# Revit family: 1STERN_FAUCET_TOUCHLESS_APOLLO_MEDICAL_F
name_source: partatom
category: Generic Models
revit_build: Autodesk Revit 2017 (Build: 20160225_1515(x64)
units: mm (PartAtom-declared; Revit-internal decimal feet)

## family parameters
Can host rebar = No
Cut with Voids When Loaded = No
Host = Face
Part Type = Normal
Room Calculation Point = Yes
Round Connector Dimension = Use Diameter
Shared = No

## types (2) — shared parameters
AVAILABLE FINISHES = Brushed Nickel - Matt Black - Satin Gold - PVD Antique Bronze - PVD rose Gold - PVD Copper - AISI316 Material
BADGE = https://bim.archiproducts.com
DEPTH = 255 mm  [stored 0.836614 ft]
Default Elevation = 1219 mm
Description = Apollo Medical F - Touch-free wall-mounted electronic faucet.‎ For hot and cold water, includes a mixer for temperature adjustment.‎ Gooseneck spout.‎ Powered by an internal 9V battery.‎ Includes a low battery indicator.‎ Adjustable settings by remote control: security time, delay in, delay out, on-off and reset to factory settings.‎
FINISHING MATERIAL = Chrome - Stern
HEIGHT = 260 mm  [stored 0.853018 ft]
INSTALLATION = Exposed wall mounted
MATERIAL DESCRIPTION = Finish: Chrome
Manufacturer = Stern Engineering
OPERATING PRESSURE = 0.5 - 5.0 BAR (7- 72.5  PSI). For water pressure greater than 5.0 bar use a pressure reducing valve.
OPTIONS = Remote control (code 07100005)
PRODUCT SHEET = https://www.archiproducts.com
SECURITY TIME = 90 seconds. Adjustableby remote control.
TECHNICAL SHEET = http://www.sternfaucets.com
URL = http://www.sternfaucets.com
VOLTAGE = 9 V
WATER FLOW = 6.0 LPM
WATER SAVING OPTIONS = 4 LPM/1 GPM, 3 LPM/0.8 GPM, 1.89 LPM/0.5 GPM, 1.3 LPM/0.35 GPM - PCA spray
WATER SUPPLY = Cold or hot water
WATER TEMPERATURE = 70°C Maximum
WIDTH = 285 mm  [stored 0.935039 ft]

## per-type parameters (varying)
| type | Model | POWER SUPPLY | PRODUCT CODE |
| APOLLO MEDICAL F - 9V BATTERY | Apollo Medical FB | 9V Battery | 340530 |
| APOLLO MEDICAL F - 9V TRANSFORMER | Apollo Medical FE | 9V Transformer | 340540 |

note: [stored X ft] marks values corroborated as IEEE doubles in the binary element streams (Revit-internal decimal feet)

## geometry (parser evidence)
native form markers: Sweep x1
no freeform markers — native parametric forms only
